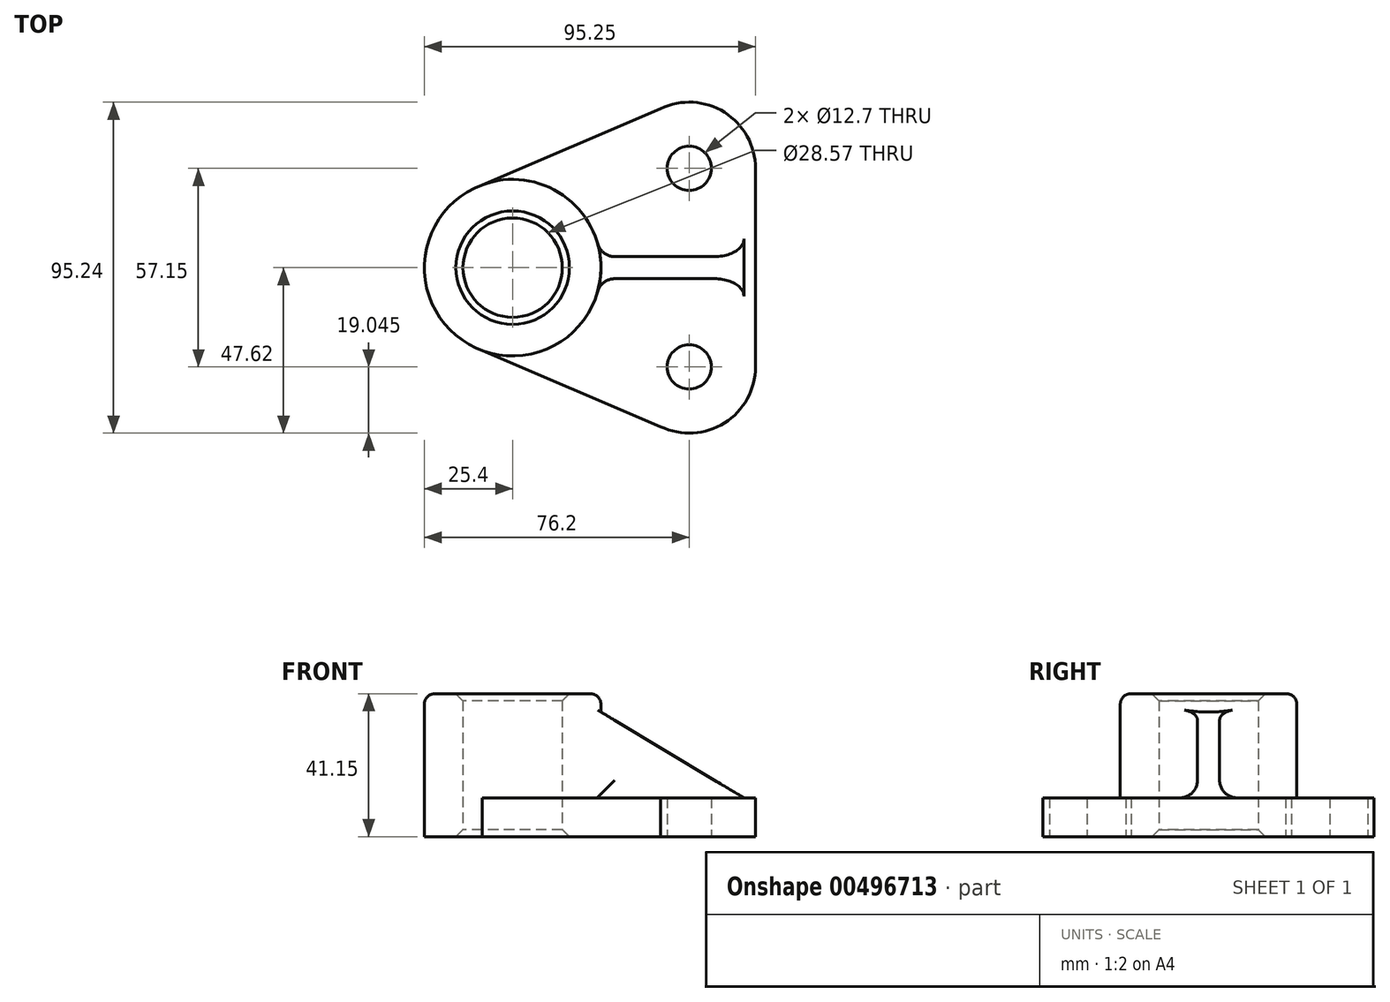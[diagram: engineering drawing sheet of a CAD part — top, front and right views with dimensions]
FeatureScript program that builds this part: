
annotation { "Feature Type Name" : "Feature", "Feature Type Description" : "" }
export const myFeature = defineFeature(function(context is Context, id is Id, definition is map)
    precondition{}
    {
        {
            var Q0;
            Q0=qCreatedBy(makeId("Top.planeOp"),FACE);
            var sketch = newSketch(context, id + "F0", { "sketchPlane" : qUnion([Q0])});
            skCircle(sketch, "E0", {"center": v(-69.85, 0) * mm, "radius": 25.4 * mm});
            skCircle(sketch, "E1", {"center": v(-69.85, 0) * mm, "radius": 14.29 * mm});
            skLineSegment(sketch, "E2", {"start": v(0, 28.57) * mm, "end": v(0, 0) * mm});
            skLineSegment(sketch, "E3.MirrorCS", {"start": v(0, -28.57) * mm, "end": v(0, 0) * mm});
            skArc(sketch, "E4.filletArc", {"start": v(-27.27, -45.76) * mm, "mid": v(-8.9, -44.7) * mm, "end": v(0, -28.58) * mm});
            skArc(sketch, "E5.filletArc", {"start": v(0, 28.57) * mm, "mid": v(-8.9, 44.7) * mm, "end": v(-27.27, 45.76) * mm});
            skCircle(sketch, "E6", {"center": v(-19.05, -28.58) * mm, "radius": 6.35 * mm});
            skCircle(sketch, "E7", {"center": v(-19.05, 28.57) * mm, "radius": 6.35 * mm});
            skLineSegment(sketch, "E8", {"start": v(-78.61, 23.84) * mm, "end": v(-27.27, 45.76) * mm});
            skLineSegment(sketch, "E9.MirrorCS", {"start": v(-78.61, -23.84) * mm, "end": v(-27.27, -45.76) * mm});
            skPoint(sketch, "E10.start.orphan", {"position": v(-69.85, 25.4) * mm});
            skPoint(sketch, "E11.MirrorCS.start.orphan", {"position": v(-69.85, -25.4) * mm});
            skSolve(sketch);
        }
        {
            var Q0;
            Q0=makeQuery(id+"F0.imprint","IMPRINT",FACE,{"disambiguationData":[TD([[makeQuery(id+"F0.imprint","IMPRINT",EDGE,{"derivedFrom":sQuery(id+"F0.wireOp",EDGE,"E1")}),-1.0]])]});
            extrude(context, id + "F1", {"entities" : qUnion([Q0]), "depth" : 41.15 * mm});
        }
        {
            var Q0;
            Q0=makeQuery(id+"F0.imprint","IMPRINT",FACE,{"disambiguationData":[TD([[makeQuery(id+"F0.imprint","IMPRINT",EDGE,{"derivedFrom":sQuery(id+"F0.wireOp",EDGE,"E2")}),-1.0]])]});
            extrude(context, id + "F2", {"entities" : qUnion([Q0]), "operationType" : NewBodyOperationType.ADD, "depth" : 11.18 * mm});
        }
        {
            var Q0;
            Q0=makeQuery(id+"F1.opExtrude","CAP_EDGE",EDGE,{"disambiguationData":[OSD([sQuery(id+"F0.wireOp",EDGE,"E0")])],"isStart":false});
            fillet(context, id + "F3", {"entities" : qUnion([Q0]), "radius" : 3.05 * mm, "tangentPropagation" : true, "allowEdgeOverflow" : false});
        }
        {
            var Q0;
            Q0=makeQuery(id+"F1.opExtrude","CAP_EDGE",EDGE,{"disambiguationData":[OSD([sQuery(id+"F0.wireOp",EDGE,"E1")])],"isStart":false});
            chamfer(context, id + "F4", {"entities" : qUnion([Q0]), "width" : 2.03 * mm, "tangentPropagation" : true});
        }
        {
            var Q0;
            Q0=makeQuery(id+"F1.opExtrude","CAP_EDGE",EDGE,{"disambiguationData":[OSD([sQuery(id+"F0.wireOp",EDGE,"E1")])],"isStart":true});
            chamfer(context, id + "F5", {"entities" : qUnion([Q0]), "width" : 2.03 * mm, "tangentPropagation" : true});
        }
        {
            var Q0;
            Q0=qCreatedBy(makeId("Front.planeOp"),FACE);
            var sketch = newSketch(context, id + "F6", { "sketchPlane" : qUnion([Q0])});
            skLineSegment(sketch, "E12", {"start": v(-45.43, 36.46) * mm, "end": v(-3.3, 11.18) * mm});
            skLineSegment(sketch, "E13", {"start": v(-45.75, 11.12) * mm, "end": v(-3.3, 11.18) * mm});
            skLineSegment(sketch, "E14", {"start": v(-45.43, 36.46) * mm, "end": v(-45.75, 11.12) * mm});
            skSolve(sketch);
        }
        {
            var Q0;
            Q0=makeQuery(id+"F6.imprint","IMPRINT",FACE,{"disambiguationData":[TD([[makeQuery(id+"F6.imprint","IMPRINT",EDGE,{"derivedFrom":sQuery(id+"F6.wireOp",EDGE,"E12")}),-1.0]])]});
            extrude(context, id + "F7", {"entities" : qUnion([Q0]), "operationType" : NewBodyOperationType.ADD, "depth" : 6.35 * mm, "symmetric" : true});
        }
        {
            var Q0;
            {var subQ0=sQuery(id+"F0.wireOp",EDGE,"E0");var subQ1=sQuery(id+"F0.wireOp",EDGE,"E9.MirrorCS");Q0=makeQuery(id+"F7.boolean.opBoolean","SPLIT",EDGE,{"disambiguationData":[TD([makeQuery(id+"F2.opExtrude","SWEPT_FACE",FACE,{"disambiguationData":[OSD([subQ1])]})])],"derivedFrom":makeQuery(id+"F2.opExtrude","CAP_EDGE",EDGE,{"disambiguationData":[OSD([subQ0])],"isStart":false})});}
            var Q1;
            Q1=makeQuery(id+"F7.boolean.opBoolean","INTERSECT",EDGE,{"derivedFrom":[makeQuery(id+"F2.opExtrude","CAP_FACE",FACE,{"disambiguationData":[OSD([sQuery(id+"F0.wireOp",EDGE,"E0"),sQuery(id+"F0.wireOp",EDGE,"E2"),sQuery(id+"F0.wireOp",EDGE,"E3.MirrorCS"),sQuery(id+"F0.wireOp",EDGE,"E4.filletArc"),sQuery(id+"F0.wireOp",EDGE,"E5.filletArc"),sQuery(id+"F0.wireOp",EDGE,"E6"),sQuery(id+"F0.wireOp",EDGE,"E7"),sQuery(id+"F0.wireOp",EDGE,"E8"),sQuery(id+"F0.wireOp",EDGE,"E9.MirrorCS")])],"isStart":false}),makeQuery(id+"F7.opExtrude","CAP_FACE",FACE,{"disambiguationData":[OSD([sQuery(id+"F6.wireOp",EDGE,"E12"),sQuery(id+"F6.wireOp",EDGE,"E13"),sQuery(id+"F6.wireOp",EDGE,"E14")])],"isStart":false})]});
            var Q2;
            {var subQ0=sQuery(id+"F0.wireOp",EDGE,"E0");var subQ1=sQuery(id+"F0.wireOp",EDGE,"E8");Q2=makeQuery(id+"F7.boolean.opBoolean","SPLIT",EDGE,{"disambiguationData":[TD([makeQuery(id+"F2.opExtrude","SWEPT_FACE",FACE,{"disambiguationData":[OSD([subQ1])]})])],"derivedFrom":makeQuery(id+"F2.opExtrude","CAP_EDGE",EDGE,{"disambiguationData":[OSD([subQ0])],"isStart":false})});}
            var Q3;
            Q3=makeQuery(id+"F7.boolean.opBoolean","INTERSECT",EDGE,{"derivedFrom":[makeQuery(id+"F2.opExtrude","CAP_FACE",FACE,{"disambiguationData":[OSD([sQuery(id+"F0.wireOp",EDGE,"E0"),sQuery(id+"F0.wireOp",EDGE,"E2"),sQuery(id+"F0.wireOp",EDGE,"E3.MirrorCS"),sQuery(id+"F0.wireOp",EDGE,"E4.filletArc"),sQuery(id+"F0.wireOp",EDGE,"E5.filletArc"),sQuery(id+"F0.wireOp",EDGE,"E6"),sQuery(id+"F0.wireOp",EDGE,"E7"),sQuery(id+"F0.wireOp",EDGE,"E8"),sQuery(id+"F0.wireOp",EDGE,"E9.MirrorCS")])],"isStart":false}),makeQuery(id+"F7.opExtrude","CAP_FACE",FACE,{"disambiguationData":[OSD([sQuery(id+"F6.wireOp",EDGE,"E12"),sQuery(id+"F6.wireOp",EDGE,"E13"),sQuery(id+"F6.wireOp",EDGE,"E14")])],"isStart":true})]});
            var Q4;
            Q4=makeQuery(id+"F7.boolean.opBoolean","INTERSECT",EDGE,{"derivedFrom":[makeQuery(id+"F1.opExtrude","SWEPT_FACE",FACE,{"disambiguationData":[OSD([sQuery(id+"F0.wireOp",EDGE,"E0")])]}),makeQuery(id+"F7.opExtrude","CAP_FACE",FACE,{"disambiguationData":[OSD([sQuery(id+"F6.wireOp",EDGE,"E12"),sQuery(id+"F6.wireOp",EDGE,"E13"),sQuery(id+"F6.wireOp",EDGE,"E14")])],"isStart":true})]});
            var Q5;
            Q5=makeQuery(id+"F7.boolean.opBoolean","INTERSECT",EDGE,{"derivedFrom":[makeQuery(id+"F1.opExtrude","SWEPT_FACE",FACE,{"disambiguationData":[OSD([sQuery(id+"F0.wireOp",EDGE,"E0")])]}),makeQuery(id+"F7.opExtrude","CAP_FACE",FACE,{"disambiguationData":[OSD([sQuery(id+"F6.wireOp",EDGE,"E12"),sQuery(id+"F6.wireOp",EDGE,"E13"),sQuery(id+"F6.wireOp",EDGE,"E14")])],"isStart":false})]});
            fillet(context, id + "F8", {"entities" : qUnion([Q0, Q1, Q2, Q3, Q4, Q5]), "radius" : 5.08 * mm, "tangentPropagation" : true, "allowEdgeOverflow" : false});
        }
    });
